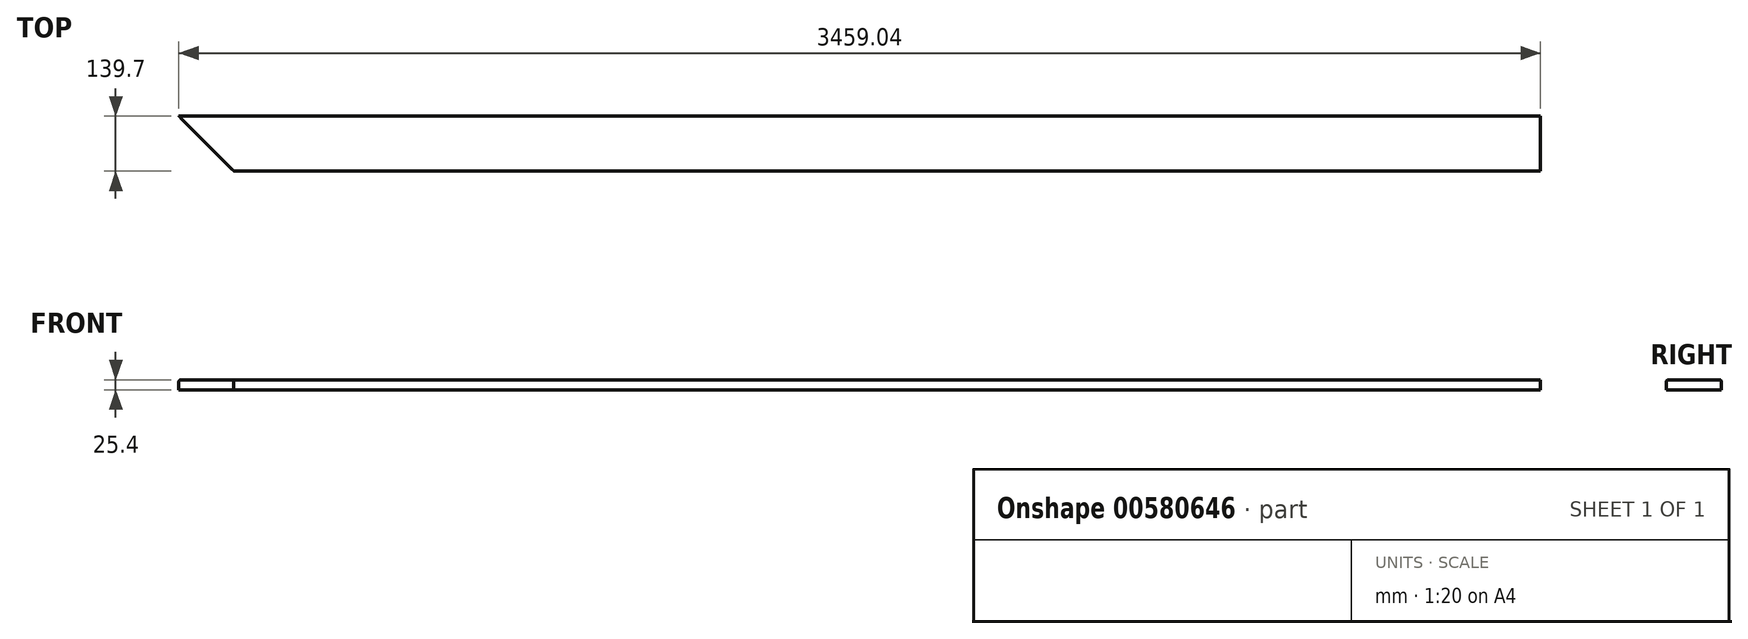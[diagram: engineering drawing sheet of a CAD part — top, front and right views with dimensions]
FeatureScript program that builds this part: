
annotation { "Feature Type Name" : "Feature", "Feature Type Description" : "" }
export const myFeature = defineFeature(function(context is Context, id is Id, definition is map)
    precondition{}
    {
        {
            var Q0;
            Q0=qCreatedBy(makeId("Top.planeOp"),FACE);
            var sketch = newSketch(context, id + "F0", { "sketchPlane" : qUnion([Q0])});
            skLineSegment(sketch, "E0.bottom", {"start": v(1729.52, -69.85) * mm, "end": v(-1589.82, -69.85) * mm});
            skLineSegment(sketch, "E0.top", {"start": v(1729.52, 69.85) * mm, "end": v(-1729.52, 69.85) * mm});
            skLineSegment(sketch, "E0.left", {"start": v(1729.52, -69.85) * mm, "end": v(1729.52, 69.85) * mm});
            skPoint(sketch, "E0.middle", {"position": v(0, 0) * mm});
            skLineSegment(sketch, "E1", {"start": v(-1729.52, 69.85) * mm, "end": v(-1589.82, -69.85) * mm});
            skSolve(sketch);
        }
        {
            var Q0;
            Q0=makeQuery(id+"F0.imprint","IMPRINT",FACE,{"disambiguationData":[TD([[makeQuery(id+"F0.imprint","IMPRINT",EDGE,{"derivedFrom":sQuery(id+"F0.wireOp",EDGE,"E0.bottom")}),-1.0]])]});
            extrude(context, id + "F1", {"entities" : qUnion([Q0]), "depth" : 25.4 * mm, "offsetDistance" : 25.4 * mm});
        }
        {
            var Q0;
            Q0=makeQuery(id+"F1.opExtrude","CAP_EDGE",EDGE,{"disambiguationData":[OSD([sQuery(id+"F0.wireOp",EDGE,"E0.top")])],"isStart":false});
            var Q1;
            Q1=makeQuery(id+"F1.opExtrude","CAP_EDGE",EDGE,{"disambiguationData":[OSD([sQuery(id+"F0.wireOp",EDGE,"E0.bottom")])],"isStart":false});
            fillet(context, id + "F2", {"entities" : qUnion([Q0, Q1]), "radius" : 5.08 * mm, "tangentPropagation" : true, "allowEdgeOverflow" : false});
        }
    });
